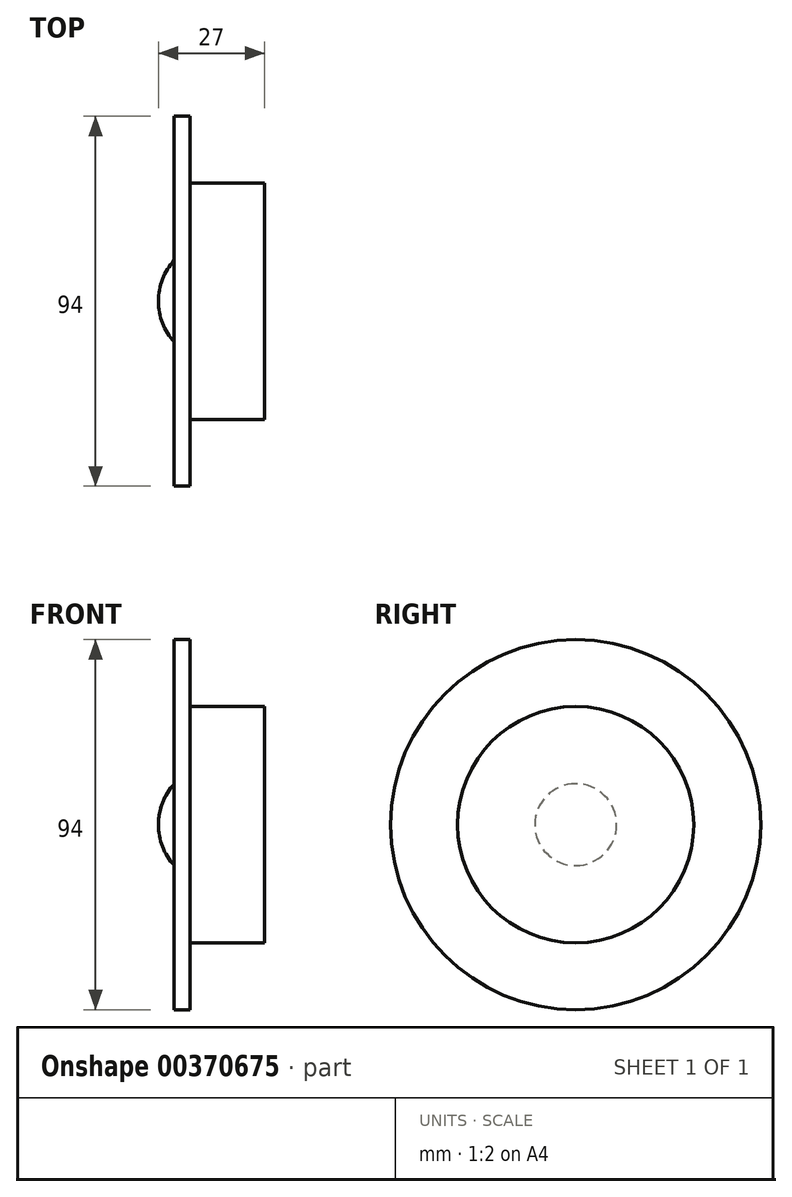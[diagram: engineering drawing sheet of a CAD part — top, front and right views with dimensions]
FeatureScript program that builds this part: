
annotation { "Feature Type Name" : "Feature", "Feature Type Description" : "" }
export const myFeature = defineFeature(function(context is Context, id is Id, definition is map)
    precondition{}
    {
        {
            var Q0;
            Q0=qCreatedBy(makeId("Front.planeOp"),FACE);
            var sketch = newSketch(context, id + "F0", { "sketchPlane" : qUnion([Q0])});
            skLineSegment(sketch, "E0", {"start": v(0, 10.4) * mm, "end": v(0, 47) * mm});
            skLineSegment(sketch, "E1", {"start": v(0, 47) * mm, "end": v(4, 47) * mm});
            skLineSegment(sketch, "E2", {"start": v(4, 47) * mm, "end": v(4, 30) * mm});
            skLineSegment(sketch, "E3", {"start": v(4, 30) * mm, "end": v(23, 30) * mm});
            skLineSegment(sketch, "E4", {"start": v(23, 30) * mm, "end": v(23, 0) * mm});
            skLineSegment(sketch, "E5", {"start": v(23, 0) * mm, "end": v(0, 0) * mm});
            skArc(sketch, "E6", {"start": v(-4, 0) * mm, "mid": v(-2.97, 5.57) * mm, "end": v(0, 10.4) * mm});
            skLineSegment(sketch, "E7", {"start": v(-4, 0) * mm, "end": v(0, 0) * mm});
            skSolve(sketch);
        }
        {
            var Q0;
            Q0=qSketchRegion(id+"F0",true);
            var Q1;
            Q1=sQuery(id+"F0.wireOp",EDGE,"E5");
            revolve(context, id + "F1", {"entities" : qUnion([Q0]), "axis" : qUnion([Q1]), "revolveType" : RevolveType.FULL});
        }
    });
